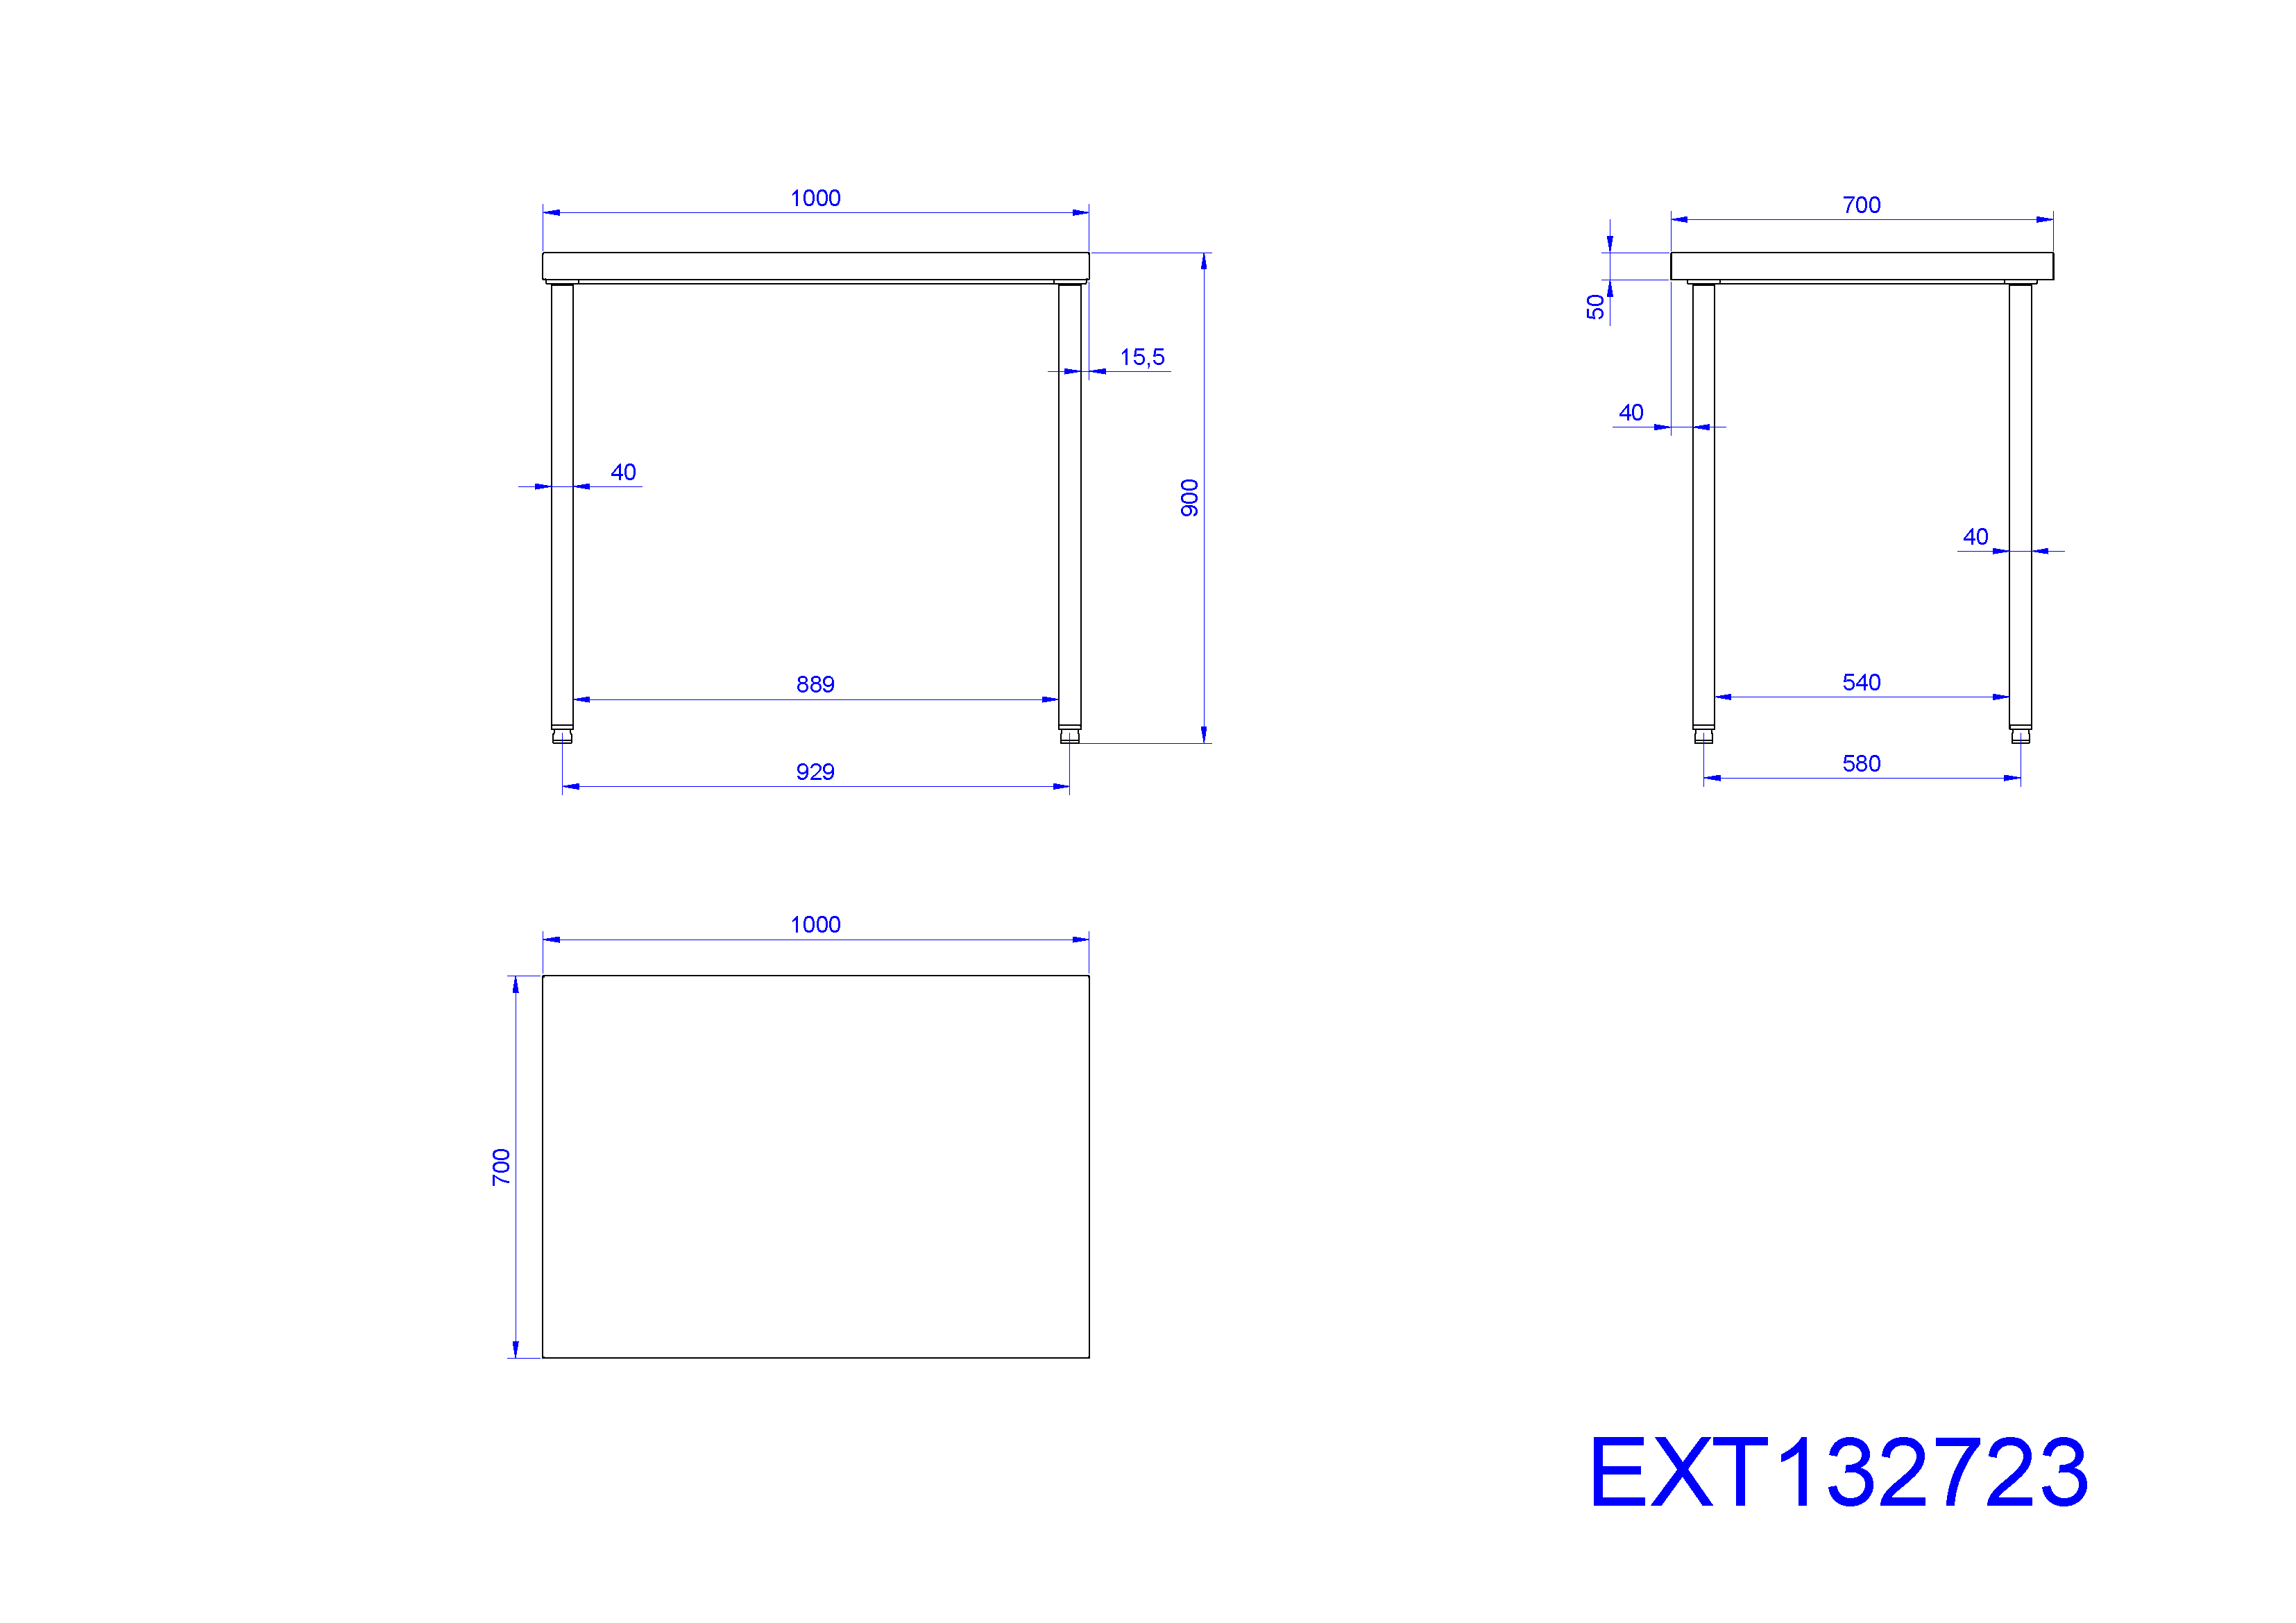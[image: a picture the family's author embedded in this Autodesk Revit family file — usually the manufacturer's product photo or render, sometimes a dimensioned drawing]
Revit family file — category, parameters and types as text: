
# Revit family: QF_ELECTROLUXPROFESSIONAL_132920_ML2S1817LN
name_source: partatom
category: Attrezzature speciali
units: mm (PartAtom-declared; Revit-internal decimal feet)

## family parameters
Basato su piano di lavoro = No
Condiviso = No
Punto di calcolo locali = No
Quota connettore circolare = Usa diametro
Sempre verticale = Sì
Taglio con vuoti quando caricato = No
Tipo di parte = Normale

## types (1)
- Standard
    Accessory = Sì
    Cold Water Size = 0 mm
    Compressed Air Pressure = 0.0 Pa
    Compressed Air Size = 0 mm
    Compressed Air Volume = 0.0 L/s
    Condensate Return Size = 0 mm
    Cycle = 0 Hz
    Depth Actual = 700 mm  [stored 2.29659 ft]
    Descrizione = CUPB.SINK 2 BOWLS(500X500)L/H DRAIN.1800
    Direct Waste Size = 140 mm
    Gas Input Pressure = 0
    Gas KW = 0
    Gas Size = 0 mm
    HP = 0 HP
    Height Actual = 1000 mm  [stored 3.28084 ft]
    Hot Water Size = 0 mm
    Item Number = 132920
    Length Actual = 1800 mm  [stored 5.90551 ft]
    Modello = ML2S1817LN
    Phase = 0
    Produttore = Electrolux Professional
    Prospetto di default = 0 mm  [stored 0 ft]
    Refrigerant Compressor Remote = Sì
    Refrigeration Liquid Line Size = 0 mm  [stored 0 ft]
    Refrigeration Suction Line Size = 0 mm  [stored 0 ft]
    Steam Consumption per Hour = 0
    Steam Supply Maximum Pressure = 0.0 Pa
    Steam Supply Minimum Pressure = 0.0 Pa
    Steam Supply Size = 0 mm
    URL = https://www.electroluxprofessional.com
    URL Manufacturer = https://www.electroluxprofessional.com
    Volts = 0 V
    Watts = 0 W
    Weight = 70.00 kg

note: source unit labels omitted for Gas Input Pressure — the stored unit's dimension contradicts the parameter name (converter mislabeling)

note: [stored X ft] marks values corroborated as IEEE doubles in the binary element streams (Revit-internal decimal feet)

## geometry (parser evidence)
native form markers: Blend x4, Sweep x5
no freeform markers — native parametric forms only
